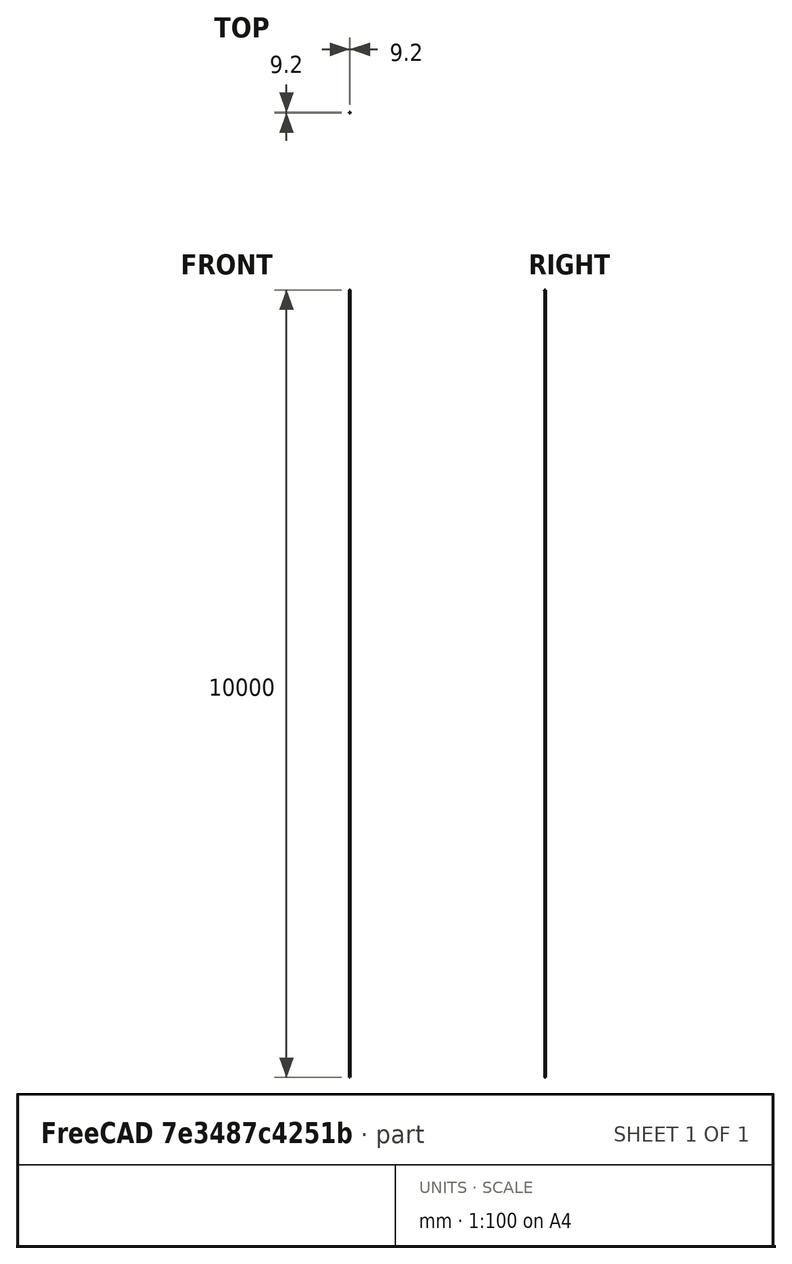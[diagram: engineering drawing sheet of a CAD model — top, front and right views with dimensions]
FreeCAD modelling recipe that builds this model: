
FCSTD DOCUMENT  (FreeCAD 0.16R)
Label: 6mm bushing
License: All rights reserved
LicenseURL: http://en.wikipedia.org/wiki/All_rights_reserved
objects: Sketcher::SketchObject×2, PartDesign::Pad×1, PartDesign::Pocket×1, Mesh::Feature×1
note: 6 computed .brp shape members not serialized (recipe doc carries the construction recipe); baked Part::Feature solids carry a one-line shape summary decoded from their .brp

FEATURE [Sketcher::SketchObject] Sketch
  sketch-geometry (1):
    g0: Circle CenterX=0 CenterY=0 CenterZ=0 NormalX=0 NormalY=0 NormalZ=1 Radius=4.6
  constraints (2):
    c: Radius(g0) = 4.6
    c: Coincident(g0,g-1)
FEATURE [PartDesign::Pad] Pad
  Length = 5.5
  Length2 = 100
  Sketch = -> Sketch
  Type = 0
FEATURE [Sketcher::SketchObject] Sketch001
  Placement = pos=(0,0,5.5) rot=(0,0,1;0rad)
  Support = -> Pad [Face3]
  sketch-geometry (1):
    g0: Circle CenterX=0 CenterY=0 CenterZ=0 NormalX=0 NormalY=0 NormalZ=1 Radius=3.15
  constraints (2):
    c: Radius(g0) = 3.15
    c: Coincident(g0,g-1)
FEATURE [PartDesign::Pocket] Pocket
  Length = 5
  Sketch = -> Sketch001
  Type = 1
FEATURE [Mesh::Feature] Mesh  label="Pocket (Meshed)"
